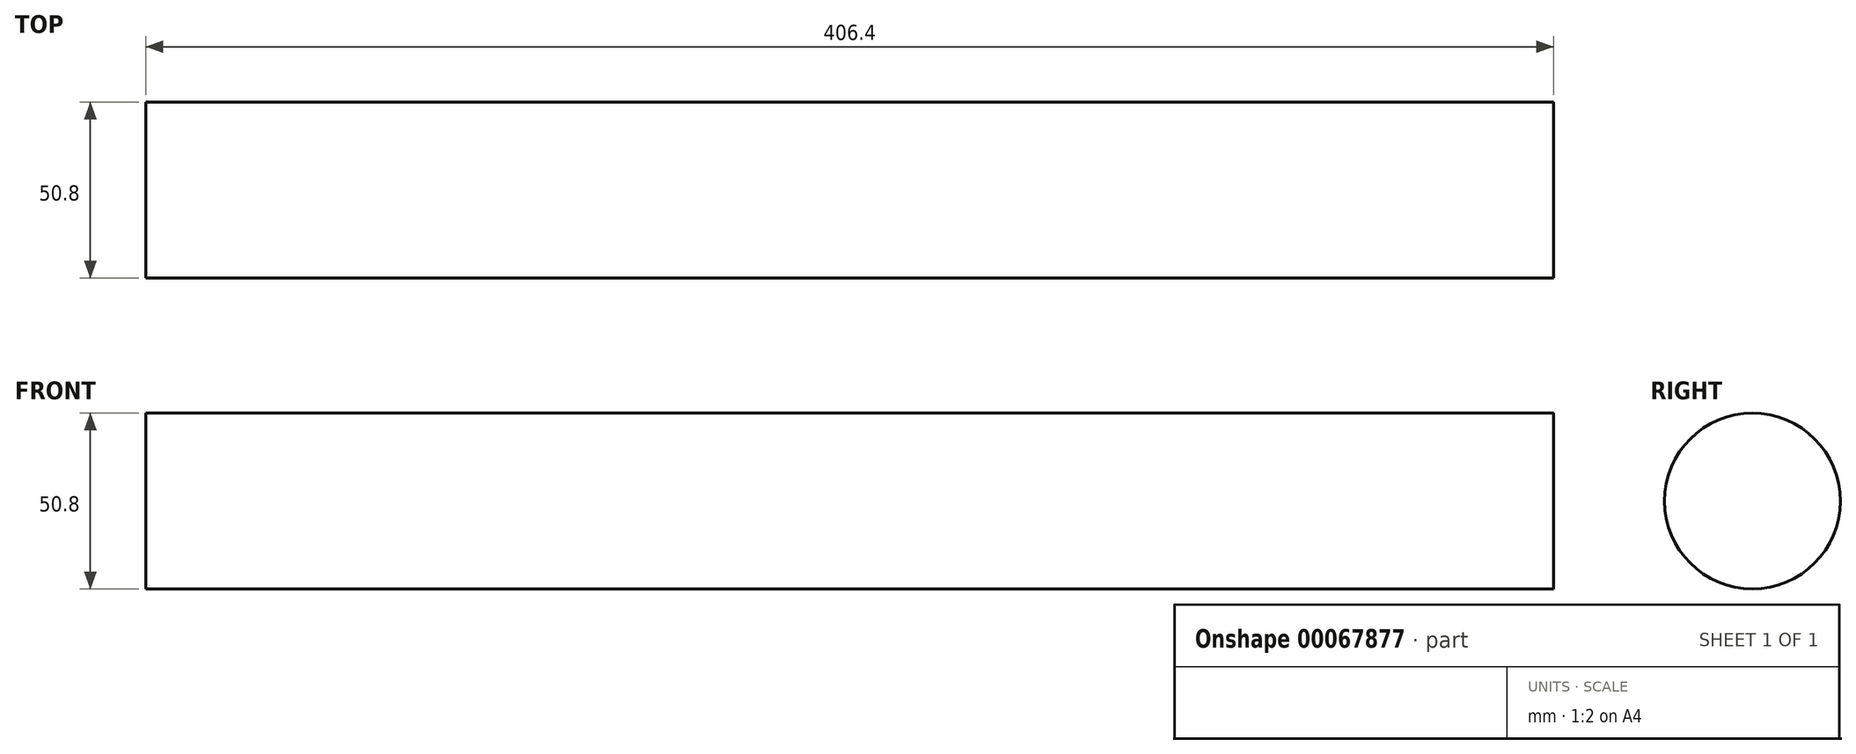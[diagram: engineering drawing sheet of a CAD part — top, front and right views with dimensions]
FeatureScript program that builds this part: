
annotation { "Feature Type Name" : "Feature", "Feature Type Description" : "" }
export const myFeature = defineFeature(function(context is Context, id is Id, definition is map)
    precondition{}
    {
        {
            var Q0;
            Q0=qCreatedBy(makeId("Right.planeOp"),FACE);
            var sketch = newSketch(context, id + "F0", { "sketchPlane" : qUnion([Q0])});
            skCircle(sketch, "E0", {"center": v(0, 0) * mm, "radius": 25.4 * mm});
            skSolve(sketch);
        }
        {
            var Q0;
            Q0=sQuery(id+"F0.wireOp",EDGE,"E0");
            extrude(context, id + "F1", {"bodyType" : ToolBodyType.SURFACE, "surfaceEntities" : qUnion([Q0]), "depth" : 406.4 * mm});
        }
    });
